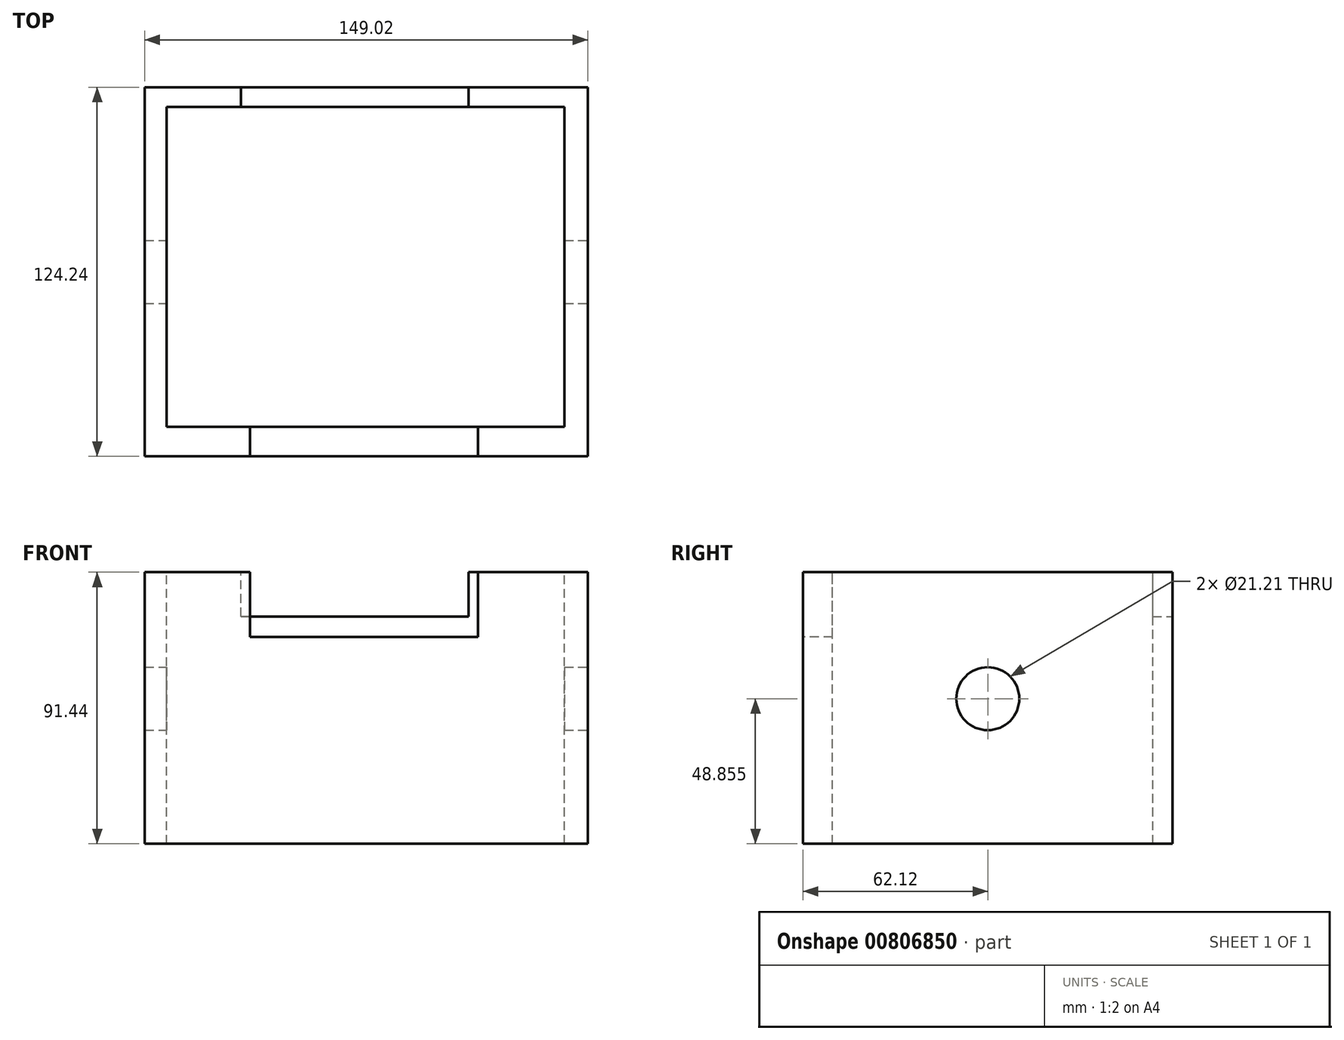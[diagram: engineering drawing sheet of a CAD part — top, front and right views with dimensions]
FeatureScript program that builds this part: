
annotation { "Feature Type Name" : "Feature", "Feature Type Description" : "" }
export const myFeature = defineFeature(function(context is Context, id is Id, definition is map)
    precondition{}
    {
        {
            var Q0;
            Q0=qCreatedBy(makeId("Top.planeOp"),FACE);
            var sketch = newSketch(context, id + "F0", { "sketchPlane" : qUnion([Q0])});
            skLineSegment(sketch, "E0.bottom", {"start": v(-74.51, 62.12) * mm, "end": v(74.51, 62.12) * mm});
            skLineSegment(sketch, "E0.top", {"start": v(-74.51, -62.12) * mm, "end": v(74.51, -62.12) * mm});
            skLineSegment(sketch, "E0.left", {"start": v(-74.51, 62.12) * mm, "end": v(-74.51, -62.12) * mm});
            skLineSegment(sketch, "E0.right", {"start": v(74.51, 62.12) * mm, "end": v(74.51, -62.12) * mm});
            skPoint(sketch, "E0.middle", {"position": v(0, 0) * mm});
            skSolve(sketch);
        }
        {
            var Q0;
            Q0 = qSketchRegion(id + "F0", true);
            extrude(context, id + "F1", {"entities" : qUnion([Q0]), "depth" : 91.44 * mm, "offsetDistance" : 25.4 * mm});
        }
        {
            var Q0;
            Q0=makeQuery(id+"F1.opExtrude","CAP_FACE",FACE,{"disambiguationData":[OSD([sQuery(id+"F0.wireOp",EDGE,"E0.bottom"),sQuery(id+"F0.wireOp",EDGE,"E0.top"),sQuery(id+"F0.wireOp",EDGE,"E0.left"),sQuery(id+"F0.wireOp",EDGE,"E0.right")])],"isStart":false});
            var sketch = newSketch(context, id + "F2", { "sketchPlane" : qUnion([Q0])});
            skLineSegment(sketch, "E1", {"start": v(-67.24, 55.53) * mm, "end": v(66.67, 55.53) * mm});
            skLineSegment(sketch, "E2", {"start": v(66.67, 55.53) * mm, "end": v(66.67, -52.23) * mm});
            skLineSegment(sketch, "E3", {"start": v(66.67, -52.23) * mm, "end": v(-67.24, -52.23) * mm});
            skLineSegment(sketch, "E4", {"start": v(-67.24, -52.23) * mm, "end": v(-67.24, 55.53) * mm});
            skSolve(sketch);
        }
        {
            var Q0;
            Q0=makeQuery(id+"F2.imprint","IMPRINT",FACE,{"disambiguationData":[TD([[makeQuery(id+"F2.imprint","IMPRINT",EDGE,{"derivedFrom":sQuery(id+"F2.wireOp",EDGE,"E1")}),-1.0]])]});
            extrude(context, id + "F3", {"entities" : qUnion([Q0]), "operationType" : NewBodyOperationType.REMOVE, "endBound" : BoundingType.THROUGH_ALL, "oppositeDirection" : true, "depth" : 55.88 * mm, "offsetDistance" : 25.4 * mm});
        }
        {
            var Q0;
            Q0=makeQuery(id+"F1.opExtrude","SWEPT_FACE",FACE,{"disambiguationData":[OSD([sQuery(id+"F0.wireOp",EDGE,"E0.top")])]});
            var sketch = newSketch(context, id + "F4", { "sketchPlane" : qUnion([Q0])});
            skLineSegment(sketch, "E5", {"start": v(-39.11, 91.44) * mm, "end": v(-39.11, 69.64) * mm});
            skLineSegment(sketch, "E6", {"start": v(-39.11, 69.64) * mm, "end": v(37.57, 69.64) * mm});
            skLineSegment(sketch, "E7", {"start": v(37.57, 69.64) * mm, "end": v(37.57, 91.44) * mm});
            skLineSegment(sketch, "E8", {"start": v(37.57, 91.44) * mm, "end": v(-39.11, 91.44) * mm});
            skSolve(sketch);
        }
        {
            var Q0;
            Q0 = qSketchRegion(id + "F4", true);
            var Q1;
            Q1=makeQuery(id+"F4.imprint","IMPRINT",FACE,{"disambiguationData":[TD([[makeQuery(id+"F4.imprint","IMPRINT",EDGE,{"derivedFrom":sQuery(id+"F4.wireOp",EDGE,"E5")}),1.0]])]});
            extrude(context, id + "F5", {"entities" : qUnion([Q0, Q1]), "operationType" : NewBodyOperationType.REMOVE, "oppositeDirection" : true, "depth" : 25.4 * mm, "offsetDistance" : 25.4 * mm});
        }
        {
            var Q0;
            Q0=makeQuery(id+"F1.opExtrude","SWEPT_FACE",FACE,{"disambiguationData":[OSD([sQuery(id+"F0.wireOp",EDGE,"E0.bottom")])]});
            var sketch = newSketch(context, id + "F6", { "sketchPlane" : qUnion([Q0])});
            skLineSegment(sketch, "E9", {"start": v(-34.41, 91.44) * mm, "end": v(-34.41, 76.52) * mm});
            skLineSegment(sketch, "E10", {"start": v(-34.41, 76.52) * mm, "end": v(42.14, 76.52) * mm});
            skLineSegment(sketch, "E11", {"start": v(42.14, 76.52) * mm, "end": v(42.14, 91.44) * mm});
            skLineSegment(sketch, "E12", {"start": v(42.14, 91.44) * mm, "end": v(-34.41, 91.44) * mm});
            skSolve(sketch);
        }
        {
            var Q0;
            Q0 = qSketchRegion(id + "F6", true);
            extrude(context, id + "F7", {"entities" : qUnion([Q0]), "operationType" : NewBodyOperationType.REMOVE, "oppositeDirection" : true, "depth" : 25.4 * mm, "offsetDistance" : 25.4 * mm});
        }
        {
            var Q0;
            Q0=makeQuery(id+"F1.opExtrude","SWEPT_FACE",FACE,{"disambiguationData":[OSD([sQuery(id+"F0.wireOp",EDGE,"E0.right")])]});
            var sketch = newSketch(context, id + "F8", { "sketchPlane" : qUnion([Q0])});
            skCircle(sketch, "E13", {"center": v(0, 48.86) * mm, "radius": 10.6 * mm});
            skCircle(sketch, "E14", {"center": v(70.66, 33.08) * mm, "radius": 14.47 * mm});
            skSolve(sketch);
        }
        {
            var Q0;
            Q0=makeQuery(id+"F8.imprint","IMPRINT",FACE,{"disambiguationData":[TD([[makeQuery(id+"F8.imprint","IMPRINT",EDGE,{"derivedFrom":sQuery(id+"F8.wireOp",EDGE,"E13")}),1.0]])]});
            extrude(context, id + "F9", {"entities" : qUnion([Q0]), "operationType" : NewBodyOperationType.REMOVE, "endBound" : BoundingType.THROUGH_ALL, "oppositeDirection" : true, "depth" : 25.4 * mm, "offsetDistance" : 25.4 * mm});
        }
    });
